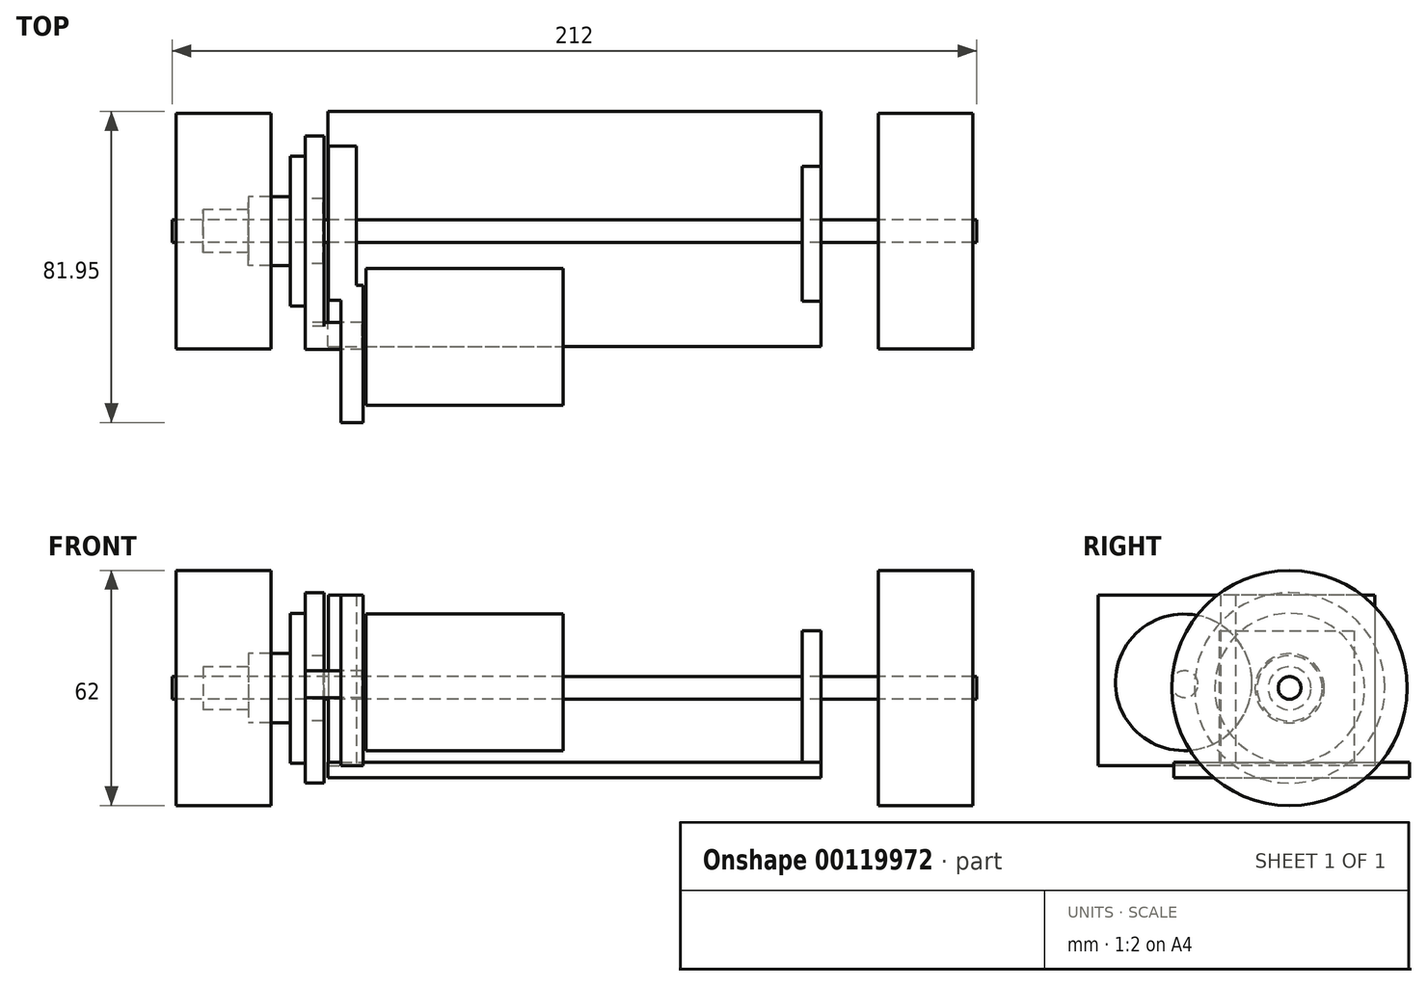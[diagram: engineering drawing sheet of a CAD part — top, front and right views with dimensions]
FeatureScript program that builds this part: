
annotation { "Feature Type Name" : "Feature", "Feature Type Description" : "" }
export const myFeature = defineFeature(function(context is Context, id is Id, definition is map)
    precondition{}
    {
        {
            var Q0;
            Q0=qCreatedBy(makeId("Top.planeOp"),FACE);
            cPlane(context, id + "F0", {"entities" : qUnion([Q0]), "cplaneType" : CPlaneType.OFFSET, "offset" : 7.5 * mm, "width" : 150 * mm, "height" : 150 * mm});
        }
        {
            var Q0;
            Q0=qCreatedBy(makeId("Right.planeOp"),FACE);
            var sketch = newSketch(context, id + "F1", { "sketchPlane" : qUnion([Q0])});
            skCircle(sketch, "E0", {"center": v(0, 31) * mm, "radius": 31 * mm});
            skSolve(sketch);
        }
        {
            var Q0;
            Q0=makeQuery(id+"F1.imprint","IMPRINT",FACE,{"disambiguationData":[TD([[makeQuery(id+"F1.imprint","IMPRINT",EDGE,{"derivedFrom":sQuery(id+"F1.wireOp",EDGE,"E0")}),1.0]])]});
            var Q1;
            Q1=sQuery(id+"F1.wireOp",EDGE,"E0");
            extrude(context, id + "F2", {"entities" : qUnion([Q0]), "surfaceEntities" : qUnion([Q1]), "depth" : 25 * mm});
        }
        {
            var Q0;
            Q0=makeQuery(id+"F2.opExtrude","SWEPT_BODY",BODY,{"disambiguationData":[OSD([sQuery(id+"F1.wireOp",EDGE,"E0")])]});
            transform(context, id + "F3", {"entities" : qUnion([Q0]), "transformType" : TransformType.TRANSLATION_3D, "dx" : 80 * mm, "dy" : 0 * mm, "dz" : 0 * mm, "makeCopy" : false});
        }
        {
            var Q0;
            Q0=makeQuery(id+"F2.opExtrude","SWEPT_BODY",BODY,{"disambiguationData":[OSD([sQuery(id+"F1.wireOp",EDGE,"E0")])]});
            var Q1;
            Q1=qCreatedBy(makeId("Right.planeOp"),FACE);
            mirror(context, id + "F4", {"entities" : qUnion([Q0]), "mirrorPlane" : qUnion([Q1])});
        }
        {
            var Q0;
            Q0=qCreatedBy(makeId("Right.planeOp"),FACE);
            var sketch = newSketch(context, id + "F5", { "sketchPlane" : qUnion([Q0])});
            skCircle(sketch, "E1", {"center": v(0, 31) * mm, "radius": 3 * mm});
            skSolve(sketch);
        }
        {
            var Q0;
            Q0=makeQuery(id+"F5.imprint","IMPRINT",FACE,{"disambiguationData":[TD([[makeQuery(id+"F5.imprint","IMPRINT",EDGE,{"derivedFrom":sQuery(id+"F5.wireOp",EDGE,"E1")}),1.0]])]});
            extrude(context, id + "F6", {"entities" : qUnion([Q0]), "endBound" : BoundingType.SYMMETRIC, "depth" : 212 * mm});
        }
        {
            var Q0;
            Q0=qCreatedBy(makeId("Right.planeOp"),FACE);
            var sketch = newSketch(context, id + "F7", { "sketchPlane" : qUnion([Q0])});
            skCircle(sketch, "E2", {"center": v(0, 31) * mm, "radius": 25.1 * mm});
            skSolve(sketch);
        }
        {
            var Q0;
            Q0=makeQuery(id+"F7.imprint","IMPRINT",FACE,{"disambiguationData":[TD([[makeQuery(id+"F7.imprint","IMPRINT",EDGE,{"derivedFrom":sQuery(id+"F7.wireOp",EDGE,"E2")}),1.0]])]});
            extrude(context, id + "F8", {"entities" : qUnion([Q0]), "depth" : 5 * mm});
        }
        {
            var Q0;
            Q0=makeQuery(id+"F8.opExtrude","SWEPT_BODY",BODY,{"disambiguationData":[OSD([sQuery(id+"F7.wireOp",EDGE,"E2")])]});
            transform(context, id + "F9", {"entities" : qUnion([Q0]), "transformType" : TransformType.TRANSLATION_3D, "dx" : -76 * mm, "dy" : 0 * mm, "dz" : 0 * mm, "makeCopy" : false});
        }
        {
            var Q0;
            Q0=qCreatedBy(makeId("Right.planeOp"),FACE);
            var sketch = newSketch(context, id + "F10", { "sketchPlane" : qUnion([Q0])});
            skLineSegment(sketch, "E3.bottom", {"start": v(-30.47, 7.35) * mm, "end": v(31.53, 7.35) * mm});
            skLineSegment(sketch, "E3.top", {"start": v(-30.47, 11.35) * mm, "end": v(31.53, 11.35) * mm});
            skLineSegment(sketch, "E3.left", {"start": v(-30.47, 7.35) * mm, "end": v(-30.47, 11.35) * mm});
            skLineSegment(sketch, "E3.right", {"start": v(31.53, 7.35) * mm, "end": v(31.53, 11.35) * mm});
            skSolve(sketch);
        }
        {
            var Q0;
            Q0 = qSketchRegion(id + "F10", true);
            extrude(context, id + "F11", {"entities" : qUnion([Q0]), "endBound" : BoundingType.SYMMETRIC, "oppositeDirection" : true, "depth" : 130 * mm});
        }
        {
            var Q0;
            Q0=qCreatedBy(id+"F0.planeOp",FACE);
            var sketch = newSketch(context, id + "F12", { "sketchPlane" : qUnion([Q0])});
            skLineSegment(sketch, "E4.bottom", {"start": v(-69.88, 22.41) * mm, "end": v(-62.48, 22.41) * mm});
            skLineSegment(sketch, "E4.top", {"start": v(-69.88, -18.17) * mm, "end": v(-66.57, -18.17) * mm});
            skLineSegment(sketch, "E4.left", {"start": v(-69.88, 22.41) * mm, "end": v(-69.88, -18.17) * mm});
            skLineSegment(sketch, "E4.right", {"start": v(-62.48, 22.41) * mm, "end": v(-62.48, -14.26) * mm});
            skLineSegment(sketch, "E5.bottom", {"start": v(-62.48, -14.26) * mm, "end": v(-60.76, -14.26) * mm});
            skLineSegment(sketch, "E5.top", {"start": v(-66.57, -50.42) * mm, "end": v(-60.76, -50.42) * mm});
            skLineSegment(sketch, "E5.left", {"start": v(-66.57, -18.17) * mm, "end": v(-66.57, -50.42) * mm});
            skLineSegment(sketch, "E5.right", {"start": v(-60.76, -14.26) * mm, "end": v(-60.76, -50.42) * mm});
            skLineSegment(sketch, "E6.bottom", {"start": v(-63.67, -14.26) * mm, "end": v(-63.67, -14.26) * mm});
            skPoint(sketch, "E7.orphan", {"position": v(-66.57, -14.26) * mm});
            skSolve(sketch);
        }
        {
            var Q0;
            Q0 = qSketchRegion(id + "F12", true);
            extrude(context, id + "F13", {"entities" : qUnion([Q0]), "depth" : 45 * mm});
        }
        {
            var Q0;
            Q0=makeQuery(id+"F13.opExtrude","SWEPT_BODY",BODY,{"disambiguationData":[OSD([sQuery(id+"F12.wireOp",EDGE,"E4.bottom"),sQuery(id+"F12.wireOp",EDGE,"E4.top"),sQuery(id+"F12.wireOp",EDGE,"E4.left"),sQuery(id+"F12.wireOp",EDGE,"E4.right"),sQuery(id+"F12.wireOp",EDGE,"E5.bottom"),sQuery(id+"F12.wireOp",EDGE,"E5.top"),sQuery(id+"F12.wireOp",EDGE,"E5.left"),sQuery(id+"F12.wireOp",EDGE,"E5.right")])]});
            transform(context, id + "F14", {"entities" : qUnion([Q0]), "transformType" : TransformType.TRANSLATION_3D, "dx" : 0 * mm, "dy" : 0 * mm, "dz" : 3 * mm, "makeCopy" : false});
        }
        {
            var Q0;
            Q0=qCreatedBy(makeId("Right.planeOp"),FACE);
            var sketch = newSketch(context, id + "F15", { "sketchPlane" : qUnion([Q0])});
            skCircle(sketch, "E8", {"center": v(-30.88, 32.48) * mm, "radius": 18 * mm});
            skSolve(sketch);
        }
        {
            var Q0;
            Q0=makeQuery(id+"F15.imprint","IMPRINT",FACE,{"disambiguationData":[TD([[makeQuery(id+"F15.imprint","IMPRINT",EDGE,{"derivedFrom":sQuery(id+"F15.wireOp",EDGE,"E8")}),1.0]])]});
            extrude(context, id + "F16", {"entities" : qUnion([Q0]), "depth" : 52 * mm});
        }
        {
            var Q0;
            Q0=makeQuery(id+"F16.opExtrude","SWEPT_BODY",BODY,{"disambiguationData":[OSD([sQuery(id+"F15.wireOp",EDGE,"E8")])]});
            transform(context, id + "F17", {"entities" : qUnion([Q0]), "transformType" : TransformType.TRANSLATION_3D, "dx" : -60 * mm, "dy" : 0 * mm, "dz" : 0 * mm, "makeCopy" : false});
        }
        {
            var Q0;
            Q0=qCreatedBy(makeId("Right.planeOp"),FACE);
            var sketch = newSketch(context, id + "F18", { "sketchPlane" : qUnion([Q0])});
            skCircle(sketch, "E9", {"center": v(-30.62, 32) * mm, "radius": 3.53 * mm});
            skSolve(sketch);
        }
        {
            var Q0;
            Q0 = qSketchRegion(id + "F18", true);
            extrude(context, id + "F19", {"entities" : qUnion([Q0]), "depth" : 15 * mm});
        }
        {
            var Q0;
            Q0=makeQuery(id+"F19.opExtrude","SWEPT_BODY",BODY,{"disambiguationData":[OSD([sQuery(id+"F18.wireOp",EDGE,"E9")])]});
            transform(context, id + "F20", {"entities" : qUnion([Q0]), "transformType" : TransformType.TRANSLATION_3D, "dx" : -76 * mm, "dy" : 0 * mm, "dz" : 0 * mm, "makeCopy" : false});
        }
        {
            var Q0;
            Q0=makeQuery(id+"F19.opExtrude","SWEPT_BODY",BODY,{"disambiguationData":[OSD([sQuery(id+"F18.wireOp",EDGE,"E9")])]});
            var Q1;
            Q1=makeQuery(id+"F16.opExtrude","SWEPT_BODY",BODY,{"disambiguationData":[OSD([sQuery(id+"F15.wireOp",EDGE,"E8")])]});
            transform(context, id + "F21", {"entities" : qUnion([Q0, Q1]), "transformType" : TransformType.TRANSLATION_3D, "dx" : 0 * mm, "dy" : 3 * mm, "dz" : 0 * mm, "makeCopy" : false});
        }
        {
            var Q0;
            Q0=qCreatedBy(makeId("Right.planeOp"),FACE);
            var sketch = newSketch(context, id + "F22", { "sketchPlane" : qUnion([Q0])});
            skLineSegment(sketch, "E10.bottom", {"start": v(-18.42, 11.27) * mm, "end": v(17.07, 11.27) * mm});
            skLineSegment(sketch, "E10.top", {"start": v(-18.42, 46.06) * mm, "end": v(17.07, 46.06) * mm});
            skLineSegment(sketch, "E10.left", {"start": v(-18.42, 11.27) * mm, "end": v(-18.42, 46.06) * mm});
            skLineSegment(sketch, "E10.right", {"start": v(17.07, 11.27) * mm, "end": v(17.07, 46.06) * mm});
            skSolve(sketch);
        }
        {
            var Q0;
            Q0=makeQuery(id+"F22.imprint","IMPRINT",FACE,{"disambiguationData":[TD([[makeQuery(id+"F22.imprint","IMPRINT",EDGE,{"derivedFrom":sQuery(id+"F22.wireOp",EDGE,"E10.bottom")}),1.0]])]});
            extrude(context, id + "F23", {"entities" : qUnion([Q0]), "depth" : 5 * mm});
        }
        {
            var Q0;
            Q0=makeQuery(id+"F23.opExtrude","SWEPT_BODY",BODY,{"disambiguationData":[OSD([sQuery(id+"F22.wireOp",EDGE,"E10.bottom"),sQuery(id+"F22.wireOp",EDGE,"E10.top"),sQuery(id+"F22.wireOp",EDGE,"E10.left"),sQuery(id+"F22.wireOp",EDGE,"E10.right")])]});
            transform(context, id + "F24", {"entities" : qUnion([Q0]), "transformType" : TransformType.TRANSLATION_3D, "dx" : 65 * mm, "dy" : 0 * mm, "dz" : 0 * mm, "makeCopy" : false});
        }
        {
            var Q0;
            Q0=makeQuery(id+"F8.opExtrude","SWEPT_BODY",BODY,{"disambiguationData":[OSD([sQuery(id+"F7.wireOp",EDGE,"E2")])]});
            var Q1;
            Q1=makeQuery(id+"F19.opExtrude","SWEPT_BODY",BODY,{"disambiguationData":[OSD([sQuery(id+"F18.wireOp",EDGE,"E9")])]});
            var Q2;
            Q2=makeQuery(id+"F16.opExtrude","SWEPT_BODY",BODY,{"disambiguationData":[OSD([sQuery(id+"F15.wireOp",EDGE,"E8")])]});
            var Q3;
            Q3=makeQuery(id+"F13.opExtrude","SWEPT_BODY",BODY,{"disambiguationData":[OSD([sQuery(id+"F12.wireOp",EDGE,"E4.bottom"),sQuery(id+"F12.wireOp",EDGE,"E4.top"),sQuery(id+"F12.wireOp",EDGE,"E4.left"),sQuery(id+"F12.wireOp",EDGE,"E4.right"),sQuery(id+"F12.wireOp",EDGE,"E5.bottom"),sQuery(id+"F12.wireOp",EDGE,"E5.top"),sQuery(id+"F12.wireOp",EDGE,"E5.left"),sQuery(id+"F12.wireOp",EDGE,"E5.right")])]});
            transform(context, id + "F25", {"entities" : qUnion([Q0, Q1, Q2, Q3]), "transformType" : TransformType.TRANSLATION_3D, "dx" : 5 * mm, "dy" : 0 * mm, "dz" : 0 * mm, "makeCopy" : false});
        }
        {
            var Q0;
            Q0=makeQuery(id+"F23.opExtrude","SWEPT_BODY",BODY,{"disambiguationData":[OSD([sQuery(id+"F22.wireOp",EDGE,"E10.bottom"),sQuery(id+"F22.wireOp",EDGE,"E10.top"),sQuery(id+"F22.wireOp",EDGE,"E10.left"),sQuery(id+"F22.wireOp",EDGE,"E10.right")])]});
            transform(context, id + "F26", {"entities" : qUnion([Q0]), "transformType" : TransformType.TRANSLATION_3D, "dx" : -5 * mm, "dy" : 0 * mm, "dz" : 0 * mm, "makeCopy" : false});
        }
        {
            var Q0;
            Q0=qCreatedBy(makeId("Front.planeOp"),FACE);
            var sketch = newSketch(context, id + "F27", { "sketchPlane" : qUnion([Q0])});
            skLineSegment(sketch, "E11", {"start": v(-97.9, 30.92) * mm, "end": v(-66.2, 30.92) * mm});
            skLineSegment(sketch, "E12", {"start": v(-66.2, 30.92) * mm, "end": v(-66.2, 39.51) * mm});
            skLineSegment(sketch, "E13", {"start": v(-66.2, 39.51) * mm, "end": v(-70.77, 39.51) * mm});
            skLineSegment(sketch, "E14", {"start": v(-70.77, 39.51) * mm, "end": v(-70.77, 50.66) * mm});
            skLineSegment(sketch, "E15", {"start": v(-70.77, 50.66) * mm, "end": v(-74.94, 50.66) * mm});
            skLineSegment(sketch, "E16", {"start": v(-74.94, 50.66) * mm, "end": v(-74.94, 40.05) * mm});
            skLineSegment(sketch, "E17", {"start": v(-74.94, 40.05) * mm, "end": v(-85.95, 40.05) * mm});
            skLineSegment(sketch, "E18", {"start": v(-85.95, 40.05) * mm, "end": v(-85.95, 36.56) * mm});
            skLineSegment(sketch, "E19", {"start": v(-85.95, 36.56) * mm, "end": v(-97.9, 36.56) * mm});
            skLineSegment(sketch, "E20", {"start": v(-97.9, 36.56) * mm, "end": v(-97.9, 30.92) * mm});
            skSolve(sketch);
        }
        {
            var Q0;
            Q0 = qSketchRegion(id + "F27", true);
            var Q1;
            Q1=sQuery(id+"F27.wireOp",EDGE,"E11");
            revolve(context, id + "F28", {"entities" : qUnion([Q0]), "axis" : qUnion([Q1]), "revolveType" : RevolveType.FULL});
        }
    });
